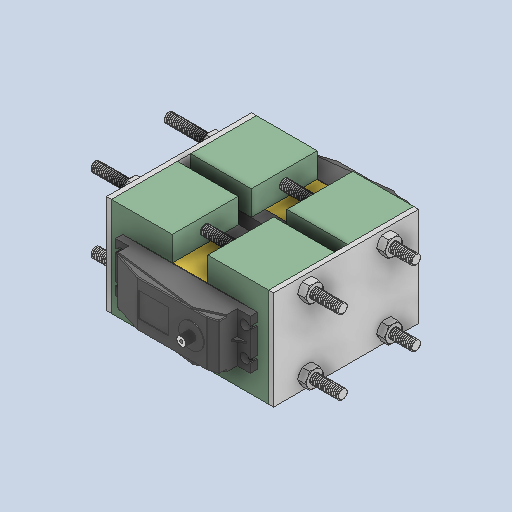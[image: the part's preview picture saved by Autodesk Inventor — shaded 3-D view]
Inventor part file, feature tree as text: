
AUTODESK INVENTOR PART (.ipt)
format: ipt  version: 2022 (Build 260153000, 153)  size: 4,858,880 bytes
history: mixed  units: in
note: dims shown in document units (in); Inventor stores cm internally (conversion verified against a paired STEP export)
features: other x16, thread x4, imported_body x1
ambient origin geometry x8: Origin, YZ Plane, XZ Plane, XY Plane, X Axis, Y Axis, Z Axis, Center Point
bodies: Solid1 (imported_parasolid), Solid2 (imported_parasolid), Solid3 (imported_parasolid), Solid4 (imported_parasolid), Solid5 (imported_parasolid), Solid6 (imported_parasolid), Solid7 (imported_parasolid), Solid8 (imported_parasolid), Solid9 (imported_parasolid), Solid10 (imported_parasolid), Solid11 (imported_parasolid), Solid12 (imported_parasolid), Solid13 (imported_parasolid), Solid14 (imported_parasolid), Solid15 (imported_parasolid), Solid16 (imported_parasolid), Solid17 (imported_parasolid), Solid18 (imported_parasolid), Solid19 (imported_parasolid), Solid20 (imported_parasolid)
feature tree (21):
  other  "servo holder"
  other  "servo holder (1)"
  other  "servo holder (2)"
  other  "servo holder (3)"
  other  "servo motor"
  other  "servo motor (1)"
  thread  "threaded rod"  [1 undecoded]
  thread  "threaded rod (1)"  [1 undecoded]
  thread  "threaded rod (2)"  [1 undecoded]
  thread  "threaded rod (3)"  [1 undecoded]
  other  "m6 nut"
  other  "m6 nut (1)"
  other  "m6 nut (2)"
  other  "m6 nut (3)"
  other  "m6 nut (4)"
  other  "m6 nut (5)"
  other  "m6 nut (6)"
  other  "m6 nut (7)"
  other  "servo mount"
  other  "servo mount bot"
  imported_body  NMx_Import_Brep_tag  [imported B-rep: ~87 faces, bbox_mm=None]
note: 4 required parameter values undecoded (feature->parameter linkage not recoverable at this tier; creation-order binding heuristic only, values carry confidence <= 0.55)
